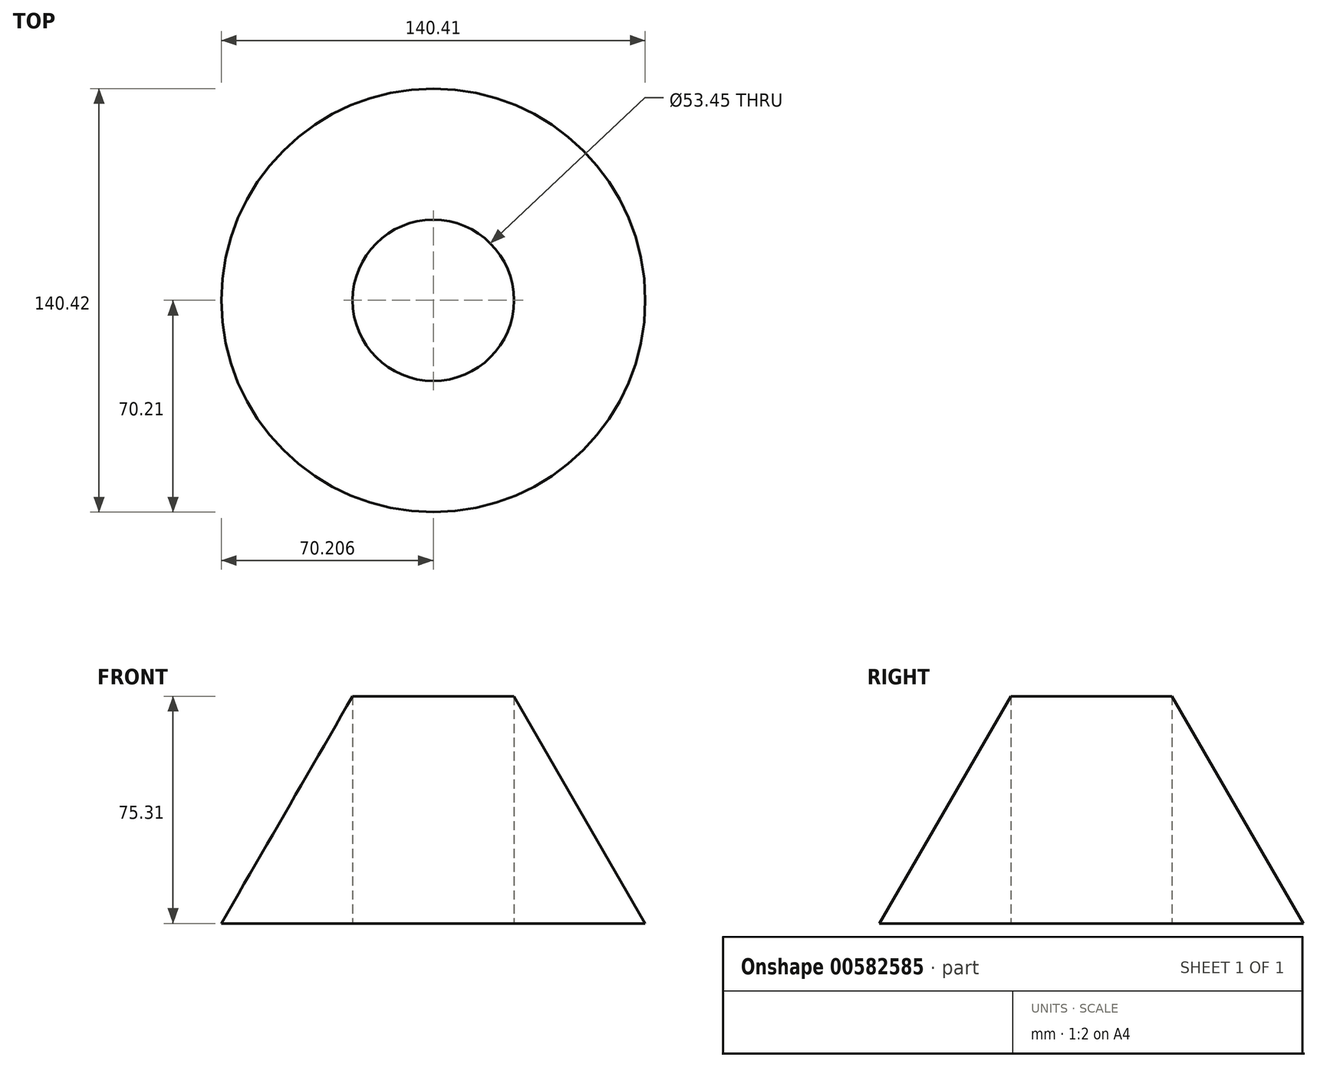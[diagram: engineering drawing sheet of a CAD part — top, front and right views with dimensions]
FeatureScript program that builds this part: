
annotation { "Feature Type Name" : "Feature", "Feature Type Description" : "" }
export const myFeature = defineFeature(function(context is Context, id is Id, definition is map)
    precondition{}
    {
        {
            var Q0;
            Q0=qCreatedBy(makeId("Front.planeOp"),FACE);
            var sketch = newSketch(context, id + "F0", { "sketchPlane" : qUnion([Q0])});
            skLineSegment(sketch, "E0", {"start": v(0, 0) * mm, "end": v(43.48, 0) * mm});
            skLineSegment(sketch, "E1", {"start": v(43.48, 0) * mm, "end": v(0, 75.31) * mm});
            skLineSegment(sketch, "E2", {"start": v(0, 75.31) * mm, "end": v(0, 0) * mm});
            skLineSegment(sketch, "E3", {"start": v(-26.72, 0) * mm, "end": v(-26.72, 45.84) * mm});
            skSolve(sketch);
        }
        {
            var Q0;
            Q0=makeQuery(id+"F0.imprint","IMPRINT",FACE,{"disambiguationData":[TD([[makeQuery(id+"F0.imprint","IMPRINT",EDGE,{"derivedFrom":sQuery(id+"F0.wireOp",EDGE,"E0")}),1.0]])]});
            var Q1;
            Q1=sQuery(id+"F0.wireOp",EDGE,"E3");
            revolve(context, id + "F1", {"entities" : qUnion([Q0]), "axis" : qUnion([Q1]), "revolveType" : RevolveType.FULL});
        }
    });
